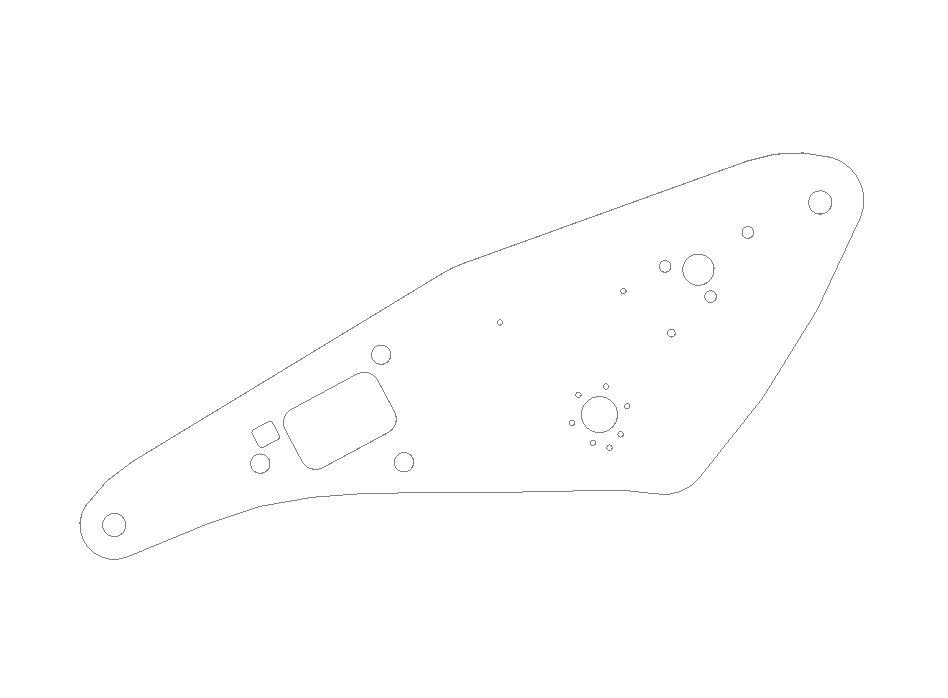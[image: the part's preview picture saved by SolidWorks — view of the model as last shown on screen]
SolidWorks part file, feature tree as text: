
SOLIDWORKS PART (.sldprt)
format: sldprt  version: not decoded by parser v0  size: 763,904 bytes
history: native  units: mm
features: sketch x10, cut_extrude x4, fillet x2, material x1, extrude x1 (+11 scaffold rows collapsed)
feature tree (29):
  scaffold x11  (default folders/planes/origin — collapsed)
  material  "Material <not specified>"
  sketch  "Sketch1"  dims[c1.D1=29.845mm c1.D14=19.177mm c1.D15=4.445mm c1.D16=~6.37032mm c1.D17=~6.37032mm c1.D2=~199.24268mm c1.D3=~156.68752mm c1.D4=406.4mm c1.D5=50.8mm c1.D6=~27.88158mm c1.D7=5.4864mm c1.D8=~29.65196mm c1.D9=~99.15144mm c1.D10=~74.00036mm c1.D11=~83.60664mm c1.D12=43.5229mm c1.D13=~46.93158mm c2.D5=50.8mm c2.D16=89.408mm c2.D17=~25.401625mm]
  sketch  "Sketch2"  dims[D7=9.652mm D1=~136.37006mm D2=~137.06094mm D3=~65.80124mm D4=~115.98402mm D5=~100.60432mm D6=~87.52586mm]
  sketch  "Sketch3"  dims[D7=16.002mm D1=~153.26868mm D2=~56.53278mm D3=~253.05004mm D4=~32.75838mm D5=~134.75462mm D6=~31.95574mm]
  sketch  "Sketch4"  dims[c1.D1=101.6mm c1.D2=50.8mm c2.D1=~187.593809mm c2.D2=~248.720597mm c3.D1=~187.59424mm c3.D2=~248.71934mm c3.D3=~8.74268mm c3.D4=2.1209mm c3.D5=86.36mm c3.D6=19.05mm c3.D7=~1094.61868mm c4.D7=28.05deg c4.D8=~16.61668mm c4.D9=54.61mm c4.D2=6.35mm]
  sketch  "Sketch5"  dims[c1.D1=~25.32761mm c1.D2=69.85mm c1.D3=263.7258mm c1.D4=~100.720305mm c1.D6=~95.355191mm c1.D8=~731.379308mm c1.D9=~32.058621mm c1.D10=~96.585496mm c1.D7=~28.07208mm c2.D6=~28.30068mm c2.D2=~731.379308mm c2.D1=~89.63152mm c2.D5=~247.693214mm c2.D7=~128.613829mm c2.D11=~89.631303mm c2.D12=~37.08194mm]
  sketch  "Sketch6"
  extrude  "Extrude1"  Depth=3.2512mm
  sketch  "Sketch7"  dims[c1.D15=16.002mm c1.D14=16.002mm c1.D16=16.002mm c1.D1=6.35mm c1.D2=19.05mm c1.D3=~16.61668mm c1.D4=86.36mm c1.D5=54.61mm c1.D6=~117.348901mm c1.D7=~31.878923mm c1.D8=~104.77653mm c1.D9=~54.921121mm c1.D10=~130.049857mm c1.D11=~67.888762mm c1.D12=~117.348901mm c2.D12=~26.580745deg c2.D13=~201.334457mm c2.D14=~33.122805mm c2.D16=~25.561602mm c3.D14=50.8mm c3.D13=50.8mm c3.D12=~117.696265mm c4.D14=~173.927029mm c4.D13=50.8mm c4.D16=40.4495mm]
  cut_extrude  "Cut-Extrude2"  [1 undecoded]
  fillet  "Fillet1"  Radius=12.7mm
  fillet  "Fillet2"  Radius=2.54mm
  sketch  "Sketch8"  dims[D2=4.4958mm D1=23.8125mm]
  cut_extrude  "Cut-Extrude3"  [1 undecoded]
  sketch  "Sketch9"  dims[D1=25.4mm D2=22.86mm]
  cut_extrude  "Cut-Extrude4"  [1 undecoded]
  sketch  "Sketch10"  dims[D1=1.5875mm]
  cut_extrude  "Cut-Extrude5"  [1 undecoded]
decode coverage: 12 of 17 modeling features carry decoded parameters
note: ~ marks probable driven/reference dimensions
note: 4 parameter values undecoded
summary: no parameter record found for 4 features
note: suppression state not decoded; provenance and decode notes live in map.json
